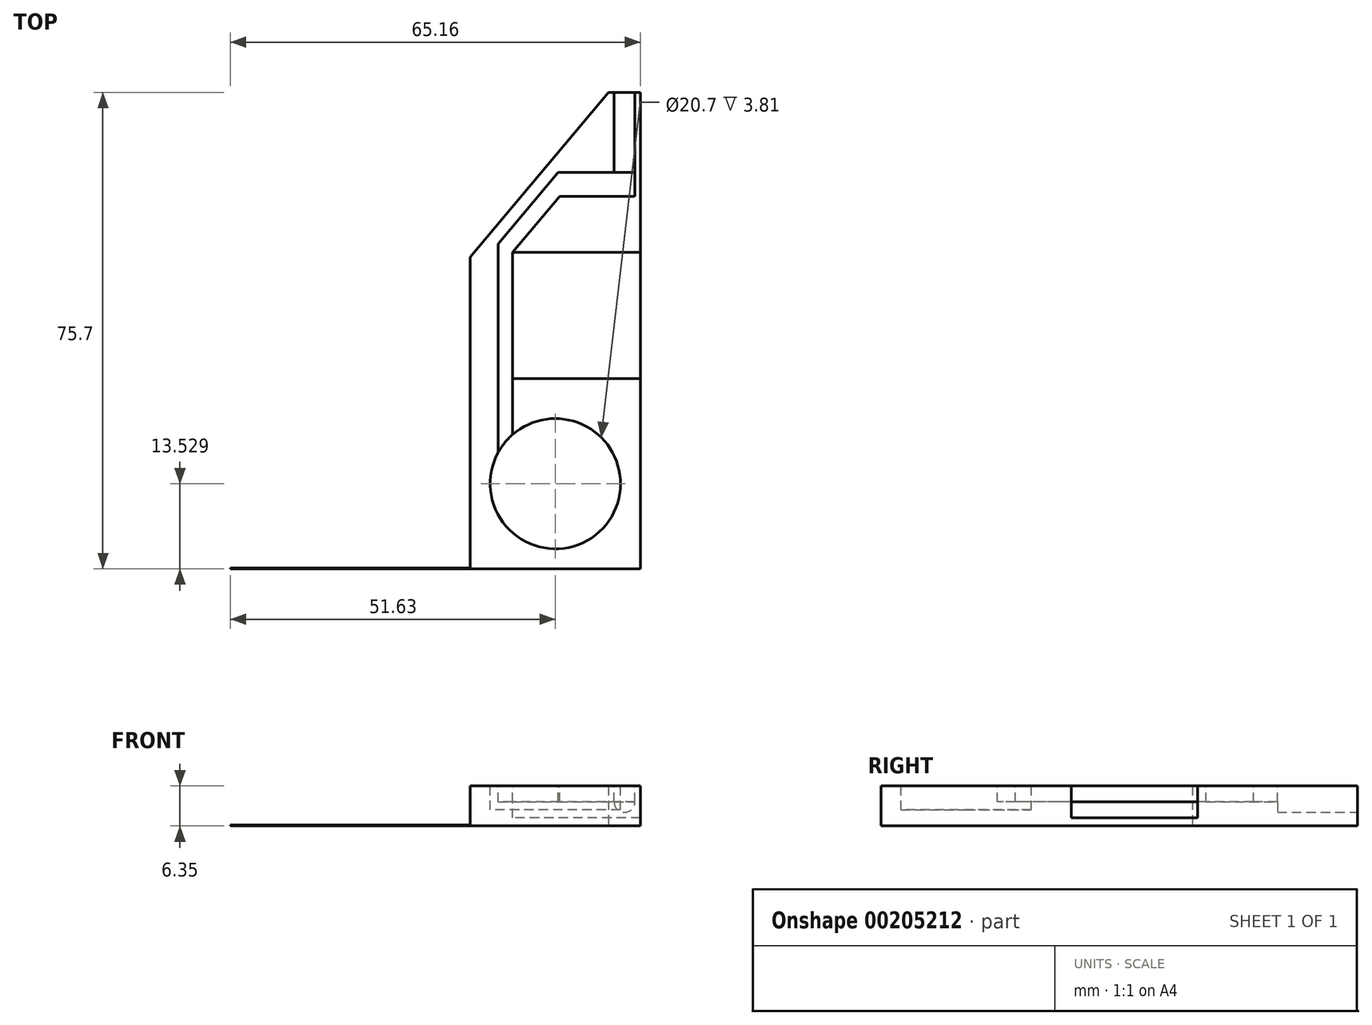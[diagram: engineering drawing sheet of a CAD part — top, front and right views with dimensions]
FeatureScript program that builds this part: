
annotation { "Feature Type Name" : "Feature", "Feature Type Description" : "" }
export const myFeature = defineFeature(function(context is Context, id is Id, definition is map)
    precondition{}
    {
        {
            var Q0;
            Q0=qCreatedBy(makeId("Top.planeOp"),FACE);
            var sketch = newSketch(context, id + "F0", { "sketchPlane" : qUnion([Q0])});
            skLineSegment(sketch, "E0", {"start": v(-13.53, 19.28) * mm, "end": v(-13.53, -30.23) * mm});
            skLineSegment(sketch, "E1", {"start": v(-13.53, 19.28) * mm, "end": v(8.45, 45.47) * mm});
            skLineSegment(sketch, "E2", {"start": v(8.45, 45.47) * mm, "end": v(13.53, 45.47) * mm});
            skLineSegment(sketch, "E3", {"start": v(13.53, 45.47) * mm, "end": v(13.53, -30.23) * mm});
            skLineSegment(sketch, "E4", {"start": v(13.53, -30.23) * mm, "end": v(-13.53, -30.23) * mm});
            skCircle(sketch, "E5", {"center": v(0, -16.7) * mm, "radius": 10.35 * mm, "construction": true});
            skLineSegment(sketch, "E6", {"start": v(-13.53, -16.7) * mm, "end": v(13.53, -16.7) * mm, "construction": true});
            skLineSegment(sketch, "E7", {"start": v(0, -30.23) * mm, "end": v(0, -16.7) * mm, "construction": true});
            skLineSegment(sketch, "E8", {"start": v(13.53, 0) * mm, "end": v(-13.53, 0) * mm, "construction": true});
            skLineSegment(sketch, "E9", {"start": v(-6.8, 0) * mm, "end": v(-6.8, 20.07) * mm, "construction": true});
            skLineSegment(sketch, "E10", {"start": v(-6.8, 20.07) * mm, "end": v(13.53, 20.07) * mm, "construction": true});
            skSolve(sketch);
        }
        {
            var Q0;
            Q0 = qSketchRegion(id + "F0", true);
            extrude(context, id + "F1", {"entities" : qUnion([Q0]), "depth" : 6.35 * mm});
        }
        {
            var Q0;
            Q0=makeQuery(id+"F1.opExtrude","CAP_FACE",FACE,{"disambiguationData":[OSD([sQuery(id+"F0.wireOp",EDGE,"E0"),sQuery(id+"F0.wireOp",EDGE,"E1"),sQuery(id+"F0.wireOp",EDGE,"E2"),sQuery(id+"F0.wireOp",EDGE,"E3"),sQuery(id+"F0.wireOp",EDGE,"E4")])],"isStart":false});
            var sketch = newSketch(context, id + "F2", { "sketchPlane" : qUnion([Q0])});
            skCircle(sketch, "E11.0", {"center": v(0, -16.7) * mm, "radius": 10.35 * mm});
            skSolve(sketch);
        }
        {
            var Q0;
            Q0=makeQuery(id+"F2.imprint","IMPRINT",FACE,{"disambiguationData":[TD([[makeQuery(id+"F2.imprint","IMPRINT",EDGE,{"derivedFrom":sQuery(id+"F2.wireOp",EDGE,"E11.0")}),1.0]])]});
            extrude(context, id + "F3", {"entities" : qUnion([Q0]), "operationType" : NewBodyOperationType.REMOVE, "oppositeDirection" : true, "depth" : 3.8 * mm});
        }
        {
            var Q0;
            Q0=makeQuery(id+"F1.opExtrude","CAP_FACE",FACE,{"disambiguationData":[OSD([sQuery(id+"F0.wireOp",EDGE,"E0"),sQuery(id+"F0.wireOp",EDGE,"E1"),sQuery(id+"F0.wireOp",EDGE,"E2"),sQuery(id+"F0.wireOp",EDGE,"E3"),sQuery(id+"F0.wireOp",EDGE,"E4")])],"isStart":false});
            var sketch = newSketch(context, id + "F4", { "sketchPlane" : qUnion([Q0])});
            skLineSegment(sketch, "E12", {"start": v(13.53, 20.07) * mm, "end": v(-6.8, 20.07) * mm});
            skLineSegment(sketch, "E13", {"start": v(-6.8, 20.07) * mm, "end": v(-6.8, 0) * mm});
            skLineSegment(sketch, "E14", {"start": v(-6.8, 0) * mm, "end": v(13.53, 0) * mm});
            skLineSegment(sketch, "E15", {"start": v(13.53, 20.07) * mm, "end": v(13.53, 0) * mm});
            skSolve(sketch);
        }
        {
            var Q0;
            Q0 = qSketchRegion(id + "F4", true);
            extrude(context, id + "F5", {"entities" : qUnion([Q0]), "operationType" : NewBodyOperationType.REMOVE, "oppositeDirection" : true, "depth" : 5.08 * mm});
        }
        {
            var Q0;
            Q0=makeQuery(id+"F1.opExtrude","SWEPT_FACE",FACE,{"disambiguationData":[OSD([sQuery(id+"F0.wireOp",EDGE,"E2")])]});
            var sketch = newSketch(context, id + "F6", { "sketchPlane" : qUnion([Q0])});
            skLineSegment(sketch, "E16", {"start": v(-10.99, 0) * mm, "end": v(-10.99, 6.35) * mm, "construction": true});
            skCircle(sketch, "E17", {"center": v(-10.99, 3.81) * mm, "radius": 1.65 * mm});
            skLineSegment(sketch, "E18", {"start": v(-9.33, 3.81) * mm, "end": v(-9.33, 6.35) * mm});
            skLineSegment(sketch, "E19", {"start": v(-12.64, 3.81) * mm, "end": v(-12.64, 6.35) * mm});
            skLineSegment(sketch, "E20", {"start": v(-12.64, 6.35) * mm, "end": v(-9.33, 6.35) * mm});
            skSolve(sketch);
        }
        {
            var Q0;
            Q0 = qSketchRegion(id + "F6", true);
            extrude(context, id + "F7", {"entities" : qUnion([Q0]), "operationType" : NewBodyOperationType.REMOVE, "oppositeDirection" : true, "depth" : 12.7 * mm});
        }
        {
            var Q0;
            Q0=makeQuery(id+"F1.opExtrude","CAP_FACE",FACE,{"disambiguationData":[OSD([sQuery(id+"F0.wireOp",EDGE,"E0"),sQuery(id+"F0.wireOp",EDGE,"E1"),sQuery(id+"F0.wireOp",EDGE,"E2"),sQuery(id+"F0.wireOp",EDGE,"E3"),sQuery(id+"F0.wireOp",EDGE,"E4")])],"isStart":false});
            var sketch = newSketch(context, id + "F8", { "sketchPlane" : qUnion([Q0])});
            skLineSegment(sketch, "E21", {"start": v(12.64, 32.77) * mm, "end": v(12.64, 28.96) * mm});
            skLineSegment(sketch, "E22", {"start": v(12.64, 28.96) * mm, "end": v(0.67, 28.96) * mm});
            skLineSegment(sketch, "E23", {"start": v(-9.08, 21.42) * mm, "end": v(0.44, 32.77) * mm});
            skLineSegment(sketch, "E24", {"start": v(0.44, 32.77) * mm, "end": v(12.64, 32.77) * mm});
            skLineSegment(sketch, "E25", {"start": v(0.67, 28.96) * mm, "end": v(-6.8, 20.07) * mm});
            skLineSegment(sketch, "E26", {"start": v(-9.08, 21.42) * mm, "end": v(-9.08, -11.73) * mm});
            skLineSegment(sketch, "E27", {"start": v(-6.8, 0) * mm, "end": v(-6.8, -8.9) * mm});
            skArc(sketch, "E28.0", {"start": v(-6.8, -8.9) * mm, "mid": v(-8.06, -10.21) * mm, "end": v(-9.08, -11.73) * mm});
            skLineSegment(sketch, "E29", {"start": v(-6.8, 20.07) * mm, "end": v(-6.8, 0) * mm});
            skSolve(sketch);
        }
        {
            var Q0;
            Q0 = qSketchRegion(id + "F8", true);
            extrude(context, id + "F9", {"entities" : qUnion([Q0]), "operationType" : NewBodyOperationType.REMOVE, "oppositeDirection" : true, "depth" : 2.54 * mm});
        }
        {
            var Q0;
            Q0=makeQuery(id+"F0.imprint","IMPRINT",FACE,{"disambiguationData":[TD([[makeQuery(id+"F0.imprint","IMPRINT",EDGE,{"derivedFrom":sQuery(id+"F0.wireOp",EDGE,"E0")}),1.0]])]});
            var sketch = newSketch(context, id + "F10", { "sketchPlane" : qUnion([Q0])});
            skLineSegment(sketch, "E30.bottom", {"start": v(-13.53, -30.23) * mm, "end": v(-51.63, -30.23) * mm});
            skLineSegment(sketch, "E30.top", {"start": v(-13.53, -30.1) * mm, "end": v(-51.63, -30.1) * mm});
            skLineSegment(sketch, "E30.left", {"start": v(-13.53, -30.23) * mm, "end": v(-13.53, -30.1) * mm});
            skLineSegment(sketch, "E30.right", {"start": v(-51.63, -30.23) * mm, "end": v(-51.63, -30.1) * mm});
            skSolve(sketch);
        }
        {
            var Q0;
            Q0 = qSketchRegion(id + "F10", true);
            extrude(context, id + "F11", {"entities" : qUnion([Q0]), "operationType" : NewBodyOperationType.ADD, "depth" : 0.13 * mm});
        }
    });
